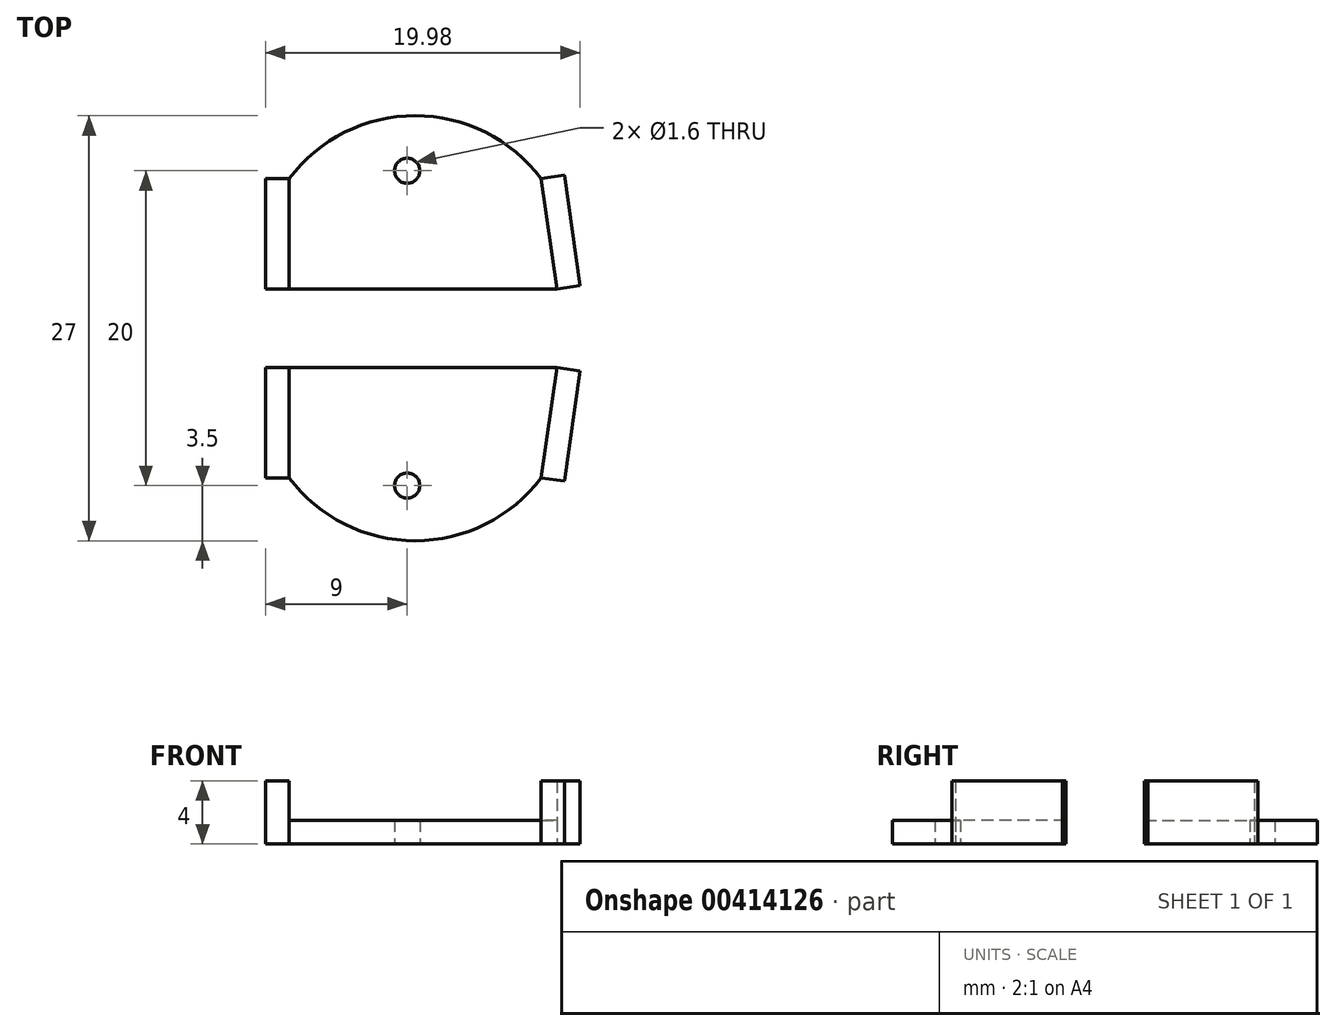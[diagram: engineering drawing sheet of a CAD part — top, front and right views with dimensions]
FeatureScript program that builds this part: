
annotation { "Feature Type Name" : "Feature", "Feature Type Description" : "" }
export const myFeature = defineFeature(function(context is Context, id is Id, definition is map)
    precondition{}
    {
        {
            var Q0;
            Q0=qCreatedBy(makeId("Top.planeOp"),FACE);
            var sketch = newSketch(context, id + "F0", { "sketchPlane" : qUnion([Q0])});
            skLineSegment(sketch, "E0", {"start": v(0, 0) * mm, "end": v(0, 7) * mm});
            skLineSegment(sketch, "E1", {"start": v(16, 7) * mm, "end": v(17, 0) * mm});
            skLineSegment(sketch, "E2", {"start": v(17, 0) * mm, "end": v(0, 0) * mm});
            skArc(sketch, "E3", {"start": v(16, 7) * mm, "mid": v(8, 11) * mm, "end": v(0, 7) * mm});
            skLineSegment(sketch, "E4.0", {"start": v(17.48, 7.21) * mm, "end": v(18.48, 0.21) * mm});
            skLineSegment(sketch, "E5", {"start": v(17.48, 7.21) * mm, "end": v(16, 7) * mm});
            skLineSegment(sketch, "E6", {"start": v(18.48, 0.21) * mm, "end": v(17, 0) * mm});
            skLineSegment(sketch, "E7.0", {"start": v(-1.5, 0) * mm, "end": v(-1.5, 7) * mm});
            skLineSegment(sketch, "E8", {"start": v(-1.5, 7) * mm, "end": v(0, 7) * mm});
            skLineSegment(sketch, "E9", {"start": v(-1.5, 0) * mm, "end": v(0, 0) * mm});
            skCircle(sketch, "E10", {"center": v(7.5, 7.5) * mm, "radius": 0.8 * mm});
            skSolve(sketch);
        }
        {
            var Q0;
            Q0=makeQuery(id+"F0.imprint","IMPRINT",FACE,{"disambiguationData":[TD([[makeQuery(id+"F0.imprint","IMPRINT",EDGE,{"derivedFrom":sQuery(id+"F0.wireOp",EDGE,"E0")}),-1.0]])]});
            extrude(context, id + "F1", {"entities" : qUnion([Q0]), "depth" : 1.5 * mm});
        }
        {
            var Q0;
            Q0=makeQuery(id+"F0.imprint","IMPRINT",FACE,{"disambiguationData":[TD([[makeQuery(id+"F0.imprint","IMPRINT",EDGE,{"derivedFrom":sQuery(id+"F0.wireOp",EDGE,"E0")}),1.0]])]});
            var Q1;
            Q1=makeQuery(id+"F0.imprint","IMPRINT",FACE,{"disambiguationData":[TD([[makeQuery(id+"F0.imprint","IMPRINT",EDGE,{"derivedFrom":sQuery(id+"F0.wireOp",EDGE,"E1")}),1.0]])]});
            extrude(context, id + "F2", {"entities" : qUnion([Q0, Q1]), "operationType" : NewBodyOperationType.ADD, "depth" : 4 * mm});
        }
        {
            var Q0;
            Q0=makeQuery(id+"F1.opExtrude","SWEPT_BODY",BODY,{"disambiguationData":[OSD([sQuery(id+"F0.wireOp",EDGE,"E0"),sQuery(id+"F0.wireOp",EDGE,"E1"),sQuery(id+"F0.wireOp",EDGE,"E2"),sQuery(id+"F0.wireOp",EDGE,"E3"),sQuery(id+"F0.wireOp",EDGE,"E10")])]});
            var Q1;
            Q1=qCreatedBy(makeId("Front.planeOp"),FACE);
            mirror(context, id + "F3", {"entities" : qUnion([Q0]), "mirrorPlane" : qUnion([Q1])});
        }
        {
            var Q0;
            Q0=makeQuery(id+"F3.opPattern","COPY",BODY,{"derivedFrom":makeQuery(id+"F1.opExtrude","SWEPT_BODY",BODY,{"disambiguationData":[OSD([sQuery(id+"F0.wireOp",EDGE,"E0"),sQuery(id+"F0.wireOp",EDGE,"E1"),sQuery(id+"F0.wireOp",EDGE,"E2"),sQuery(id+"F0.wireOp",EDGE,"E3"),sQuery(id+"F0.wireOp",EDGE,"E10")])]}),"instanceName":"1"});
            var Q1;
            Q1=sQuery(id+"F0.wireOp",EDGE,"E0");
            var Q2;
            Q2=sQuery(id+"F0.wireOp",EDGE,"E0");
            transform(context, id + "F4", {"entities" : qUnion([Q0]), "transformType" : TransformType.TRANSLATION_DISTANCE, "transformDirection" : qUnion([Q2]), "distance" : 5 * mm, "oppositeDirection" : true, "makeCopy" : false});
        }
    });
